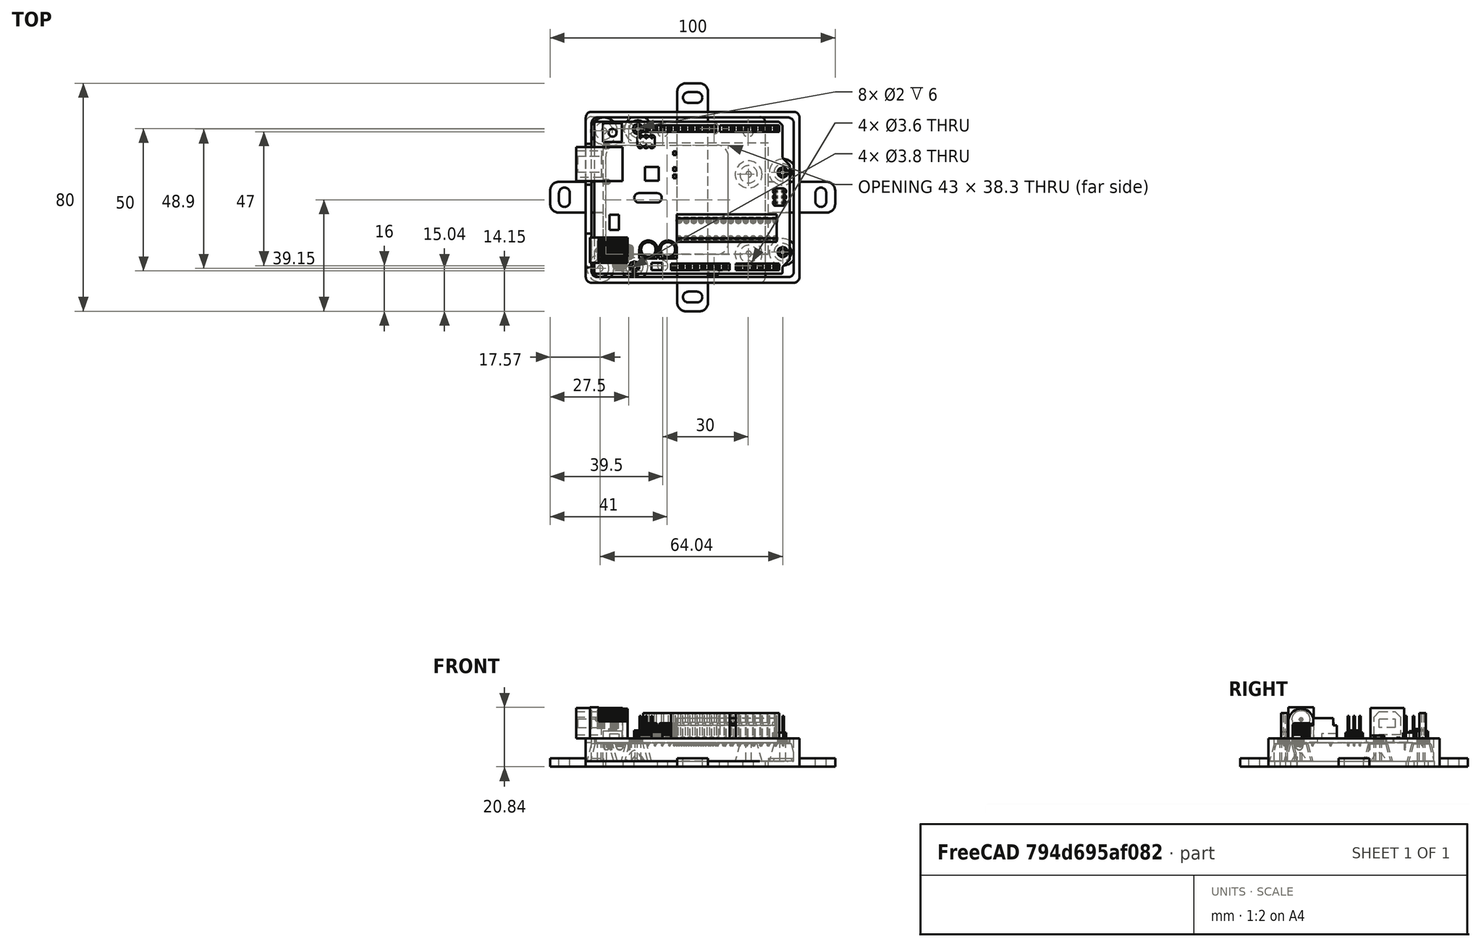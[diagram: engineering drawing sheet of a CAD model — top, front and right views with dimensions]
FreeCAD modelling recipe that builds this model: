
FCSTD DOCUMENT  (FreeCAD 0.18.4R)
Label: arduino_uno
License: All rights reserved
LicenseURL: http://en.wikipedia.org/wiki/All_rights_reserved
objects: Part::FeaturePython×8, Part::Box×7, Part::Cut×5, Part::MultiFuse×5, Part::Cylinder×4, Part::Fillet×4, Part::Feature×3, Part::Cone×2, App::MeasureDistance×2, Spreadsheet::Sheet×1, Part::Compound×1
note: 39 computed .brp shape members not serialized (recipe doc carries the construction recipe); baked Part::Feature solids carry a one-line shape summary decoded from their .brp

FEATURE [Part::Box] cube
  AttacherType = Attacher::AttachEngine3D
  Height = 10
  Length = 75
  Width = 60
FEATURE [Part::Box] cube001
  AttacherType = Attacher::AttachEngine3D
  Height = 16
  Length = 71
  Placement = pos=(2,2,2) rot=(0,0,1;0rad)
  Width = 56
FEATURE [Part::Box] cube002
  AttacherType = Attacher::AttachEngine3D
  Height = 15
  Length = 2.6
  Placement = pos=(-0.5,5.4,8.6) rot=(0,0,1;0rad)
  Width = 11.89
FEATURE [Part::Box] cube003
  AttacherType = Attacher::AttachEngine3D
  Height = 15
  Length = 2.6
  Placement = pos=(-0.5,34.4,8.6) rot=(0,0,1;0rad)
  Width = 14.43
FEATURE [Part::Cylinder] cylinder009
  Angle = 360
  AttacherType = Attacher::AttachEngine3D
  Height = 8
  Radius = 1
  expr: Radius = p.hole_r
FEATURE [Part::Box] cube006
  AttacherType = Attacher::AttachEngine3D
  Height = 17
  Length = 58
  Placement = pos=(6.1,10.1,0) rot=(0,0,1;0rad)
  Width = 39
FEATURE [Spreadsheet::Sheet] Spreadsheet  label="p"
  cells = A1=hole_r; B1(hole_r)=1; A2=box_tube_connector_hole_x_dist; B2(box_tube_connector_hole_x_dist)=30; A3=box_tube_connector_hole_y_dist; B3(box_tube_connector_hole_y_dist)=47; A4=box_tube_connector_hole_y_off; B4(box_tube_connector_hole_y_off)=6; A5=box_tube_connector_hole_x_off; B5(box_tube_connector_hole_x_off)=5; A7=attach_hole_dist; B7(attach_hole_dist)=10; A8=attach_hole_r; B8(attach_hole_r)=1.9
FEATURE [Part::FeaturePython] Point  # WARN: FeaturePython — macro-defined, semantics opaque (R4)
  X = 18.34
  Y = 53.9
  Z = 0
FEATURE [Part::FeaturePython] Point001  # WARN: FeaturePython — macro-defined, semantics opaque (R4)
  X = 17.07
  Y = 5.64
  Z = 0
FEATURE [Part::FeaturePython] Point002  # WARN: FeaturePython — macro-defined, semantics opaque (R4)
  X = 69.14
  Y = 10.72
  Z = 0
FEATURE [Part::FeaturePython] Point003  # WARN: FeaturePython — macro-defined, semantics opaque (R4)
  X = 69.14
  Y = 38.66
  Z = 0
FEATURE [Part::Compound] Compound  label="hole points compound"
  Links = -> [Point002,Point001,Point,Point003]
FEATURE [Part::Cone] Cone
  Angle = 360
  AttacherType = Attacher::AttachEngine3D
  Height = 7
  Radius1 = 5
  Radius2 = 3.05
FEATURE [Part::Cut] difference003  label="hole with stand"
  Base = -> Cone
  Placement = pos=(13.97,2.54,0) rot=(0,0,1;0rad)
  Tool = -> cylinder009
FEATURE [Part::FeaturePython] PointArray  label="hole point array"  # WARN: FeaturePython — macro-defined, semantics opaque (R4)
  Base = -> difference003
  Count = 4
  Placement = pos=(-14,-2.5,1) rot=(0,0,1;0rad)
  PointList = -> Compound
FEATURE [Part::Feature] Solid  label="Arduino"
  Placement = pos=(29.2,-5.1,40) rot=(0,0,-1;1.5708rad)
  shape: large baked B-rep (35 MB .brp); summary skipped
FEATURE [Part::Cylinder] Cylinder001  label="screw hole001"
  Angle = 360
  AttacherType = Attacher::AttachEngine3D
  Height = 20
  Radius = 1.8
FEATURE [Part::FeaturePython] Array001  label="screw hole array001"  # Draft array (typed FeaturePython)
  Angle = 360
  ArrayType = 0
  Axis = (0,0,1)
  Base = -> Cylinder001
  Center = (0,0,0)
  Fuse = false
  IntervalAxis = (0,0,0)
  IntervalX = (30,0,0)
  IntervalY = (0,47,0)
  IntervalZ = (0,0,1)
  NumberPolar = 1
  NumberX = 2
  NumberY = 2
  NumberZ = 1
  Placement = pos=(27,6,-5) rot=(0,0,1;0rad)
  expr: Placement.Base.y = p.box_tube_connector_hole_y_off
  expr: Placement.Base.x = p.box_tube_connector_hole_x_off + 22
  expr: IntervalY.y = p.box_tube_connector_hole_y_dist
  expr: IntervalX.x = p.box_tube_connector_hole_x_dist
FEATURE [Part::MultiFuse] Fusion001  label="arduino box extraction fusion"
  Shapes = -> [Array001,cube006]
FEATURE [Part::Fillet] Fillet001
  Base = -> cube
  Edges = 4 edges r=2: [Edge1,Edge3,Edge5,Edge7]
FEATURE [Part::Fillet] Fillet002
  Base = -> cube001
  Edges = 4 edges r=2: [Edge1,Edge3,Edge5,Edge7]
FEATURE [Part::MultiFuse] union
  Shapes = -> [cube002,cube003,Fillet002]
FEATURE [Part::Cut] difference
  Base = -> Fillet001
  Tool = -> union
FEATURE [Part::Feature] Cut003001  label="attach plane x dir001"
  shape: bbox 100 x 10.8 x 3 mm, 18 faces (baked)
FEATURE [Part::MultiFuse] union003
  Shapes = -> [difference,PointArray,Cut003001]
FEATURE [Part::Cut] difference007  label="arduino box cut"
  Base = -> union003
  Tool = -> Fusion001
FEATURE [Part::Feature] Cut002001  label="attach plane y dir001"
  shape: bbox 10.8 x 80 x 3 mm, 18 faces (baked)
FEATURE [App::MeasureDistance] Distance  label="Distance: 53.37 mm"
  Distance = 53.3704
  P1 = (17.4166,56.0256,9.914)
  P2 = (24.5054,3.15,8.39)
FEATURE [App::MeasureDistance] Distance001  label="Distance: 68.59 mm"
  Distance = 68.5917
  P1 = (3.04,21.6786,9.914)
  P2 = (71.62,22.9473,9.914)
FEATURE [Part::Cylinder] cylinder010
  Angle = 360
  AttacherType = Attacher::AttachEngine3D
  Height = 8
  Radius = 1
  expr: Radius = p.hole_r
FEATURE [Part::Cone] Cone001
  Angle = 360
  AttacherType = Attacher::AttachEngine3D
  Height = 7
  Radius1 = 5
  Radius2 = 3.05
FEATURE [Part::Cut] difference008  label="uno hole with stand"
  Base = -> Cone001
  Tool = -> cylinder010
FEATURE [Part::FeaturePython] PointArray001  label="uno hole point array"  # WARN: FeaturePython — macro-defined, semantics opaque (R4)
  Base = -> difference008
  Count = 4
  Placement = pos=(-12,-0.6,1) rot=(0,0,1;0rad)
  PointList = -> Compound
FEATURE [Part::Box] cube010  label="bottom_plate"
  AttacherType = Attacher::AttachEngine3D
  Height = 2
  Length = 63
  Width = 58.3
FEATURE [Part::Fillet] Fillet004  label="bottom plate fillet"
  Base = -> cube010
  Edges = 4 edges r=2: [Edge1,Edge3,Edge5,Edge7]
FEATURE [Part::Box] cube011  label="botom hole"
  AttacherType = Attacher::AttachEngine3D
  Height = 2
  Length = 43
  Placement = pos=(7,10,0) rot=(0,0,1;0rad)
  Width = 38.3
  expr: Placement.Base.y = (bottom_plate.Width - Width) / 2
  expr: Placement.Base.x = (bottom_plate.Length - Length) / 2 - 3mm
  expr: Height = bottom_plate.Height
  expr: Width = bottom_plate.Width - 20mm
  expr: Length = bottom_plate.Length - 20mm
FEATURE [Part::Fillet] Fillet  label="botom hole fillet"
  Base = -> cube011
  Edges = 4 edges r=4: [Edge1,Edge3,Edge5,Edge7]
FEATURE [Part::Cylinder] Cylinder004  label="attachment hole"
  Angle = 360
  AttacherType = Attacher::AttachEngine3D
  Height = 10
  Radius = 1.9
  expr: Radius = p.attach_hole_r
FEATURE [Part::FeaturePython] Array  label="attachment hole array"  # Draft array (typed FeaturePython)
  Angle = 360
  ArrayType = 0
  Axis = (0,0,1)
  Base = -> Cylinder004
  Center = (0,0,0)
  Fuse = false
  IntervalAxis = (0,0,0)
  IntervalX = (30,0,0)
  IntervalY = (0,50,0)
  IntervalZ = (0,0,1)
  NumberPolar = 1
  NumberX = 2
  NumberY = 2
  NumberZ = 1
  Placement = pos=(15,4.15,0) rot=(0,0,1;0rad)
  expr: Placement.Base.y = (bottom_plate.Width / 1mm - p.attach_hole_dist * 5) / 2
  expr: Placement.Base.x = p.attach_hole_dist / 2 * 3
  expr: IntervalY.y = p.attach_hole_dist * 5
  expr: IntervalX.x = p.attach_hole_dist * 3
FEATURE [Part::MultiFuse] Fusion  label="bottom extraction fusion"
  Shapes = -> [Fillet,Array]
FEATURE [Part::Cut] Cut  label="uno bottom cut"
  Base = -> Fillet004
  Tool = -> Fusion
FEATURE [Part::MultiFuse] Fusion002  label="uno plate"
  Shapes = -> [PointArray001,Cut]
